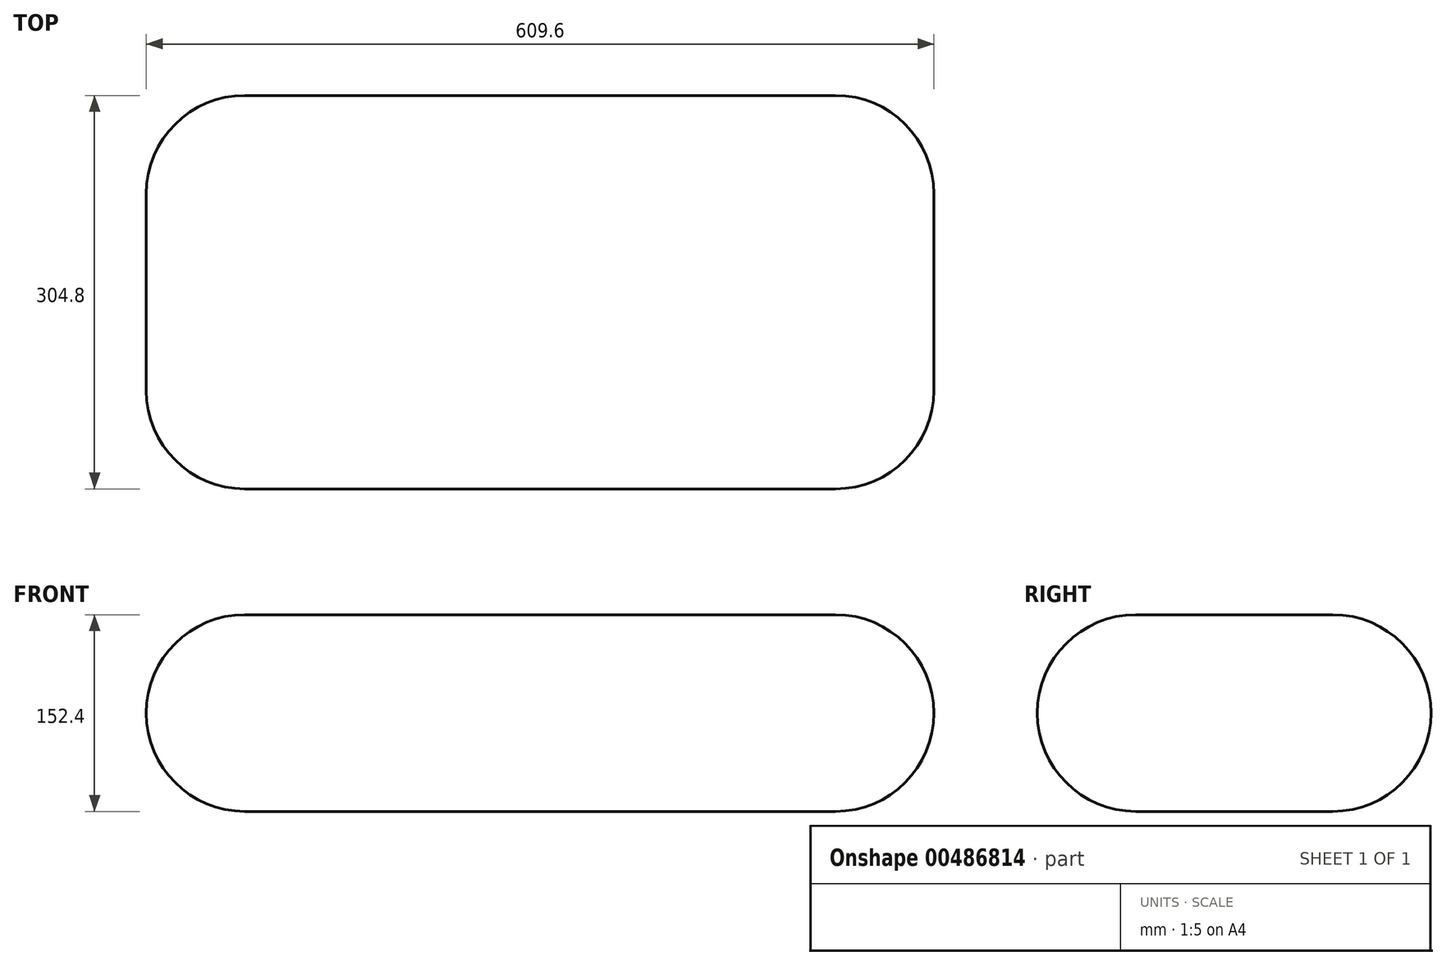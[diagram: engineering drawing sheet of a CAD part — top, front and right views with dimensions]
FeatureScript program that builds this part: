
annotation { "Feature Type Name" : "Feature", "Feature Type Description" : "" }
export const myFeature = defineFeature(function(context is Context, id is Id, definition is map)
    precondition{}
    {
        {
            var Q0;
            Q0=qCreatedBy(makeId("Top.planeOp"),FACE);
            var sketch = newSketch(context, id + "F0", { "sketchPlane" : qUnion([Q0])});
            skLineSegment(sketch, "E0.bottom", {"start": v(-107.4, -152.76) * mm, "end": v(502.2, -152.76) * mm});
            skLineSegment(sketch, "E0.top", {"start": v(-107.4, 152.04) * mm, "end": v(502.2, 152.04) * mm});
            skLineSegment(sketch, "E0.left", {"start": v(-107.4, -152.76) * mm, "end": v(-107.4, 152.04) * mm});
            skLineSegment(sketch, "E0.right", {"start": v(502.2, -152.76) * mm, "end": v(502.2, 152.04) * mm});
            skSolve(sketch);
        }
        {
            var Q0;
            Q0 = qSketchRegion(id + "F0", true);
            var Q1;
            Q1=makeQuery(id+"F0.imprint","IMPRINT",FACE,{"disambiguationData":[TD([[makeQuery(id+"F0.imprint","IMPRINT",EDGE,{"derivedFrom":sQuery(id+"F0.wireOp",EDGE,"E0.bottom")}),1.0]])]});
            extrude(context, id + "F1", {"entities" : qUnion([Q0, Q1]), "depth" : 152.4 * mm});
        }
        {
            var Q0;
            Q0=makeQuery(id+"F1.opExtrude","CAP_EDGE",EDGE,{"disambiguationData":[OSD([sQuery(id+"F0.wireOp",EDGE,"E0.bottom")])],"isStart":false});
            var Q1;
            Q1=makeQuery(id+"F1.opExtrude","CAP_EDGE",EDGE,{"disambiguationData":[OSD([sQuery(id+"F0.wireOp",EDGE,"E0.left")])],"isStart":false});
            var Q2;
            Q2=makeQuery(id+"F1.opExtrude","CAP_EDGE",EDGE,{"disambiguationData":[OSD([sQuery(id+"F0.wireOp",EDGE,"E0.top")])],"isStart":false});
            var Q3;
            Q3=makeQuery(id+"F1.opExtrude","CAP_EDGE",EDGE,{"disambiguationData":[OSD([sQuery(id+"F0.wireOp",EDGE,"E0.right")])],"isStart":false});
            var Q4;
            Q4=makeQuery(id+"F1.opExtrude","SWEPT_EDGE",EDGE,{"disambiguationData":[OSD([sQuery(id+"F0.wireOp",EDGE,"E0.bottom"),sQuery(id+"F0.wireOp",EDGE,"E0.right")])]});
            var Q5;
            Q5=makeQuery(id+"F1.opExtrude","SWEPT_EDGE",EDGE,{"disambiguationData":[OSD([sQuery(id+"F0.wireOp",EDGE,"E0.top"),sQuery(id+"F0.wireOp",EDGE,"E0.right")])]});
            var Q6;
            Q6=makeQuery(id+"F1.opExtrude","CAP_EDGE",EDGE,{"disambiguationData":[OSD([sQuery(id+"F0.wireOp",EDGE,"E0.right")])],"isStart":true});
            var Q7;
            Q7=makeQuery(id+"F1.opExtrude","CAP_EDGE",EDGE,{"disambiguationData":[OSD([sQuery(id+"F0.wireOp",EDGE,"E0.bottom")])],"isStart":true});
            var Q8;
            Q8=makeQuery(id+"F1.opExtrude","SWEPT_EDGE",EDGE,{"disambiguationData":[OSD([sQuery(id+"F0.wireOp",EDGE,"E0.bottom"),sQuery(id+"F0.wireOp",EDGE,"E0.left")])]});
            var Q9;
            Q9=makeQuery(id+"F1.opExtrude","CAP_EDGE",EDGE,{"disambiguationData":[OSD([sQuery(id+"F0.wireOp",EDGE,"E0.left")])],"isStart":true});
            var Q10;
            Q10=makeQuery(id+"F1.opExtrude","SWEPT_EDGE",EDGE,{"disambiguationData":[OSD([sQuery(id+"F0.wireOp",EDGE,"E0.top"),sQuery(id+"F0.wireOp",EDGE,"E0.left")])]});
            var Q11;
            Q11=makeQuery(id+"F1.opExtrude","CAP_EDGE",EDGE,{"disambiguationData":[OSD([sQuery(id+"F0.wireOp",EDGE,"E0.top")])],"isStart":true});
            fillet(context, id + "F2", {"entities" : qUnion([Q0, Q1, Q2, Q3, Q4, Q5, Q6, Q7, Q8, Q9, Q10, Q11]), "radius" : 76.2 * mm, "tangentPropagation" : true, "allowEdgeOverflow" : false});
        }
    });
